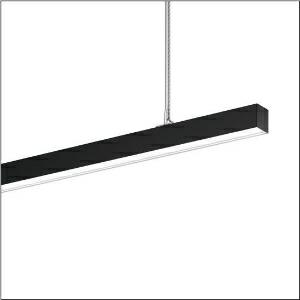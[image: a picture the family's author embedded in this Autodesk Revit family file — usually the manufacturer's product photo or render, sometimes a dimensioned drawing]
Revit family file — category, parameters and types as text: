
# Revit family: silica_21_51mx30tat4b
name_source: partatom
category: Lighting Fixtures
units: mm (PartAtom-declared; Revit-internal decimal feet)

## family parameters
Cut with Voids When Loaded = No
Host = Face
Light Source = No
Part Type = Normal
Room Calculation Point = No
Round Connector Dimension = Use Diameter
Shared = No

## types (1)
- --- (1 x LED, 4120 lm, 33.8 W, 6500K)
    Apparent Load = 34 VA
    CIE Flux Codes = 47 79 96 58 100
    Color Rendering = 80
    Color Temperature = 6500K
    Default Elevation = 1800 mm
    Description = Silica 21, office luminaire, primary optical cover: cover, of PMMA, opal, light emission: direct/indirect distribution, primary light characteristic: symmetric, installation type: suspended mounting, LED, rated luminous flux: 4.120lm, luminous efficacy: 116lm/W, light colour: 8tw, colour temperature: 2700..6500K, control gear: DALI DT8, with terminal, 3+2-pole, max. 2.5mm², mains connection: 220..240V, AC, 50/60Hz, rated input power: 35.5W, luminaire housing, of aluminium, matt jet black (RAL 9005), length: 1.204mm, width: 53mm, height: 53mm, protection rating (complete): IP20, insulation class (complete): insulation class I (protective earthing), certification: CE, permissible operating ambient temperature: 0..+35°C, standard: EN 50419, packaging unit: 1 piece
    Height = 53 mm
    Lamp = 1 x LED
    Lamp Light Flux = 4120 lm
    Lamp Power = 33.8 W
    Lamp count = 1
    Length = 1204 mm
    Luminous efficacy = 122 lm/W
    Manufacturer = Siteco
    ModVariant = No
    Model = 51MX30TAT4B
    Mounting Place = Ceiling
    Mounting Type = Pendant
    Number of Poles = 1
    OnlyDefault = Yes
    Power Factor = 1
    Product Name = Silica 21
    Product group = office luminaire | ceiling pendant
    ProductGroupID = 903
    Protection Class = Protection class I
    Protection Degree = IP 20
    RLX_Detail_Level = 1
    RLX_Emergency_Light_Flux = 0 lm
    RLX_Emergency_Type = 0
    RLX_Emergency_Type_DB = No
    RlxData = <blob elided: 22833 chars, md5=5d609dde>
    Socket = socket
    Standby Power = 0 W
    System Light Flux = 4120 lm
    System Power = 34 W
    Type Comments = individual setting
    Type Image = l_1335856.jpg
    URL = http://relux.com
    VarID = @adj_139133
    Voltage = 0 V
    Weight = 0.00 kg
    Width = 53 mm

## geometry (parser evidence)
native form markers: Blend x4, Sweep x11
no freeform markers — native parametric forms only
